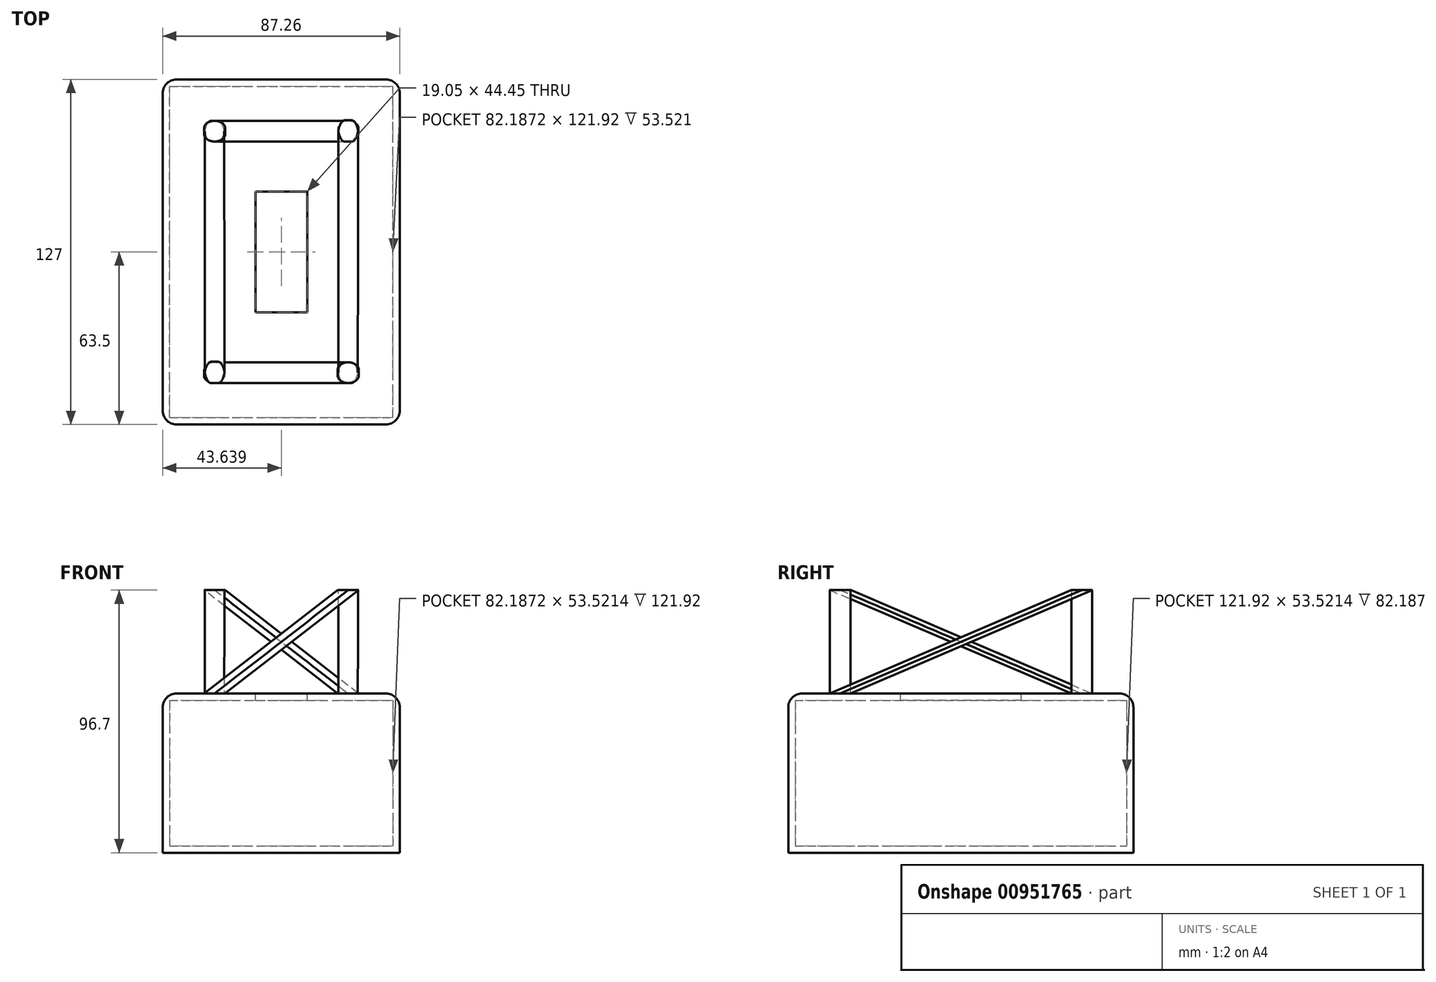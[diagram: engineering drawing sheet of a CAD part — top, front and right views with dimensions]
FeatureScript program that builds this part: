
annotation { "Feature Type Name" : "Feature", "Feature Type Description" : "" }
export const myFeature = defineFeature(function(context is Context, id is Id, definition is map)
    precondition{}
    {
        {
            var Q0;
            Q0=qCreatedBy(makeId("Front.planeOp"),FACE);
            var sketch = newSketch(context, id + "F0", { "sketchPlane" : qUnion([Q0])});
            skLineSegment(sketch, "E0.bottom", {"start": v(-42.36, 35.47) * mm, "end": v(44.9, 35.47) * mm});
            skLineSegment(sketch, "E0.top", {"start": v(-42.36, -23.13) * mm, "end": v(44.9, -23.13) * mm});
            skLineSegment(sketch, "E0.left", {"start": v(-42.36, 35.47) * mm, "end": v(-42.36, -23.13) * mm});
            skLineSegment(sketch, "E0.right", {"start": v(44.9, 35.47) * mm, "end": v(44.9, -23.13) * mm});
            skSolve(sketch);
        }
        {
            var Q0;
            Q0=makeQuery(id+"F0.imprint","IMPRINT",FACE,{"disambiguationData":[TD([[makeQuery(id+"F0.imprint","IMPRINT",EDGE,{"derivedFrom":sQuery(id+"F0.wireOp",EDGE,"E0.bottom")}),-1.0]])]});
            extrude(context, id + "F1", {"entities" : qUnion([Q0]), "depth" : 127 * mm, "offsetDistance" : 25.4 * mm});
        }
        {
            var Q0;
            Q0=makeQuery(id+"F1.opExtrude","SWEPT_FACE",FACE,{"disambiguationData":[OSD([sQuery(id+"F0.wireOp",EDGE,"E0.bottom")])]});
            var sketch = newSketch(context, id + "F2", { "sketchPlane" : qUnion([Q0])});
            skLineSegment(sketch, "E1.bottom", {"start": v(-8.25, -41.28) * mm, "end": v(10.8, -41.28) * mm});
            skLineSegment(sketch, "E1.top", {"start": v(-8.25, -85.73) * mm, "end": v(10.8, -85.73) * mm});
            skLineSegment(sketch, "E1.left", {"start": v(-8.25, -41.28) * mm, "end": v(-8.25, -85.73) * mm});
            skLineSegment(sketch, "E1.right", {"start": v(10.8, -41.28) * mm, "end": v(10.8, -85.73) * mm});
            skSolve(sketch);
        }
        {
            var Q0;
            Q0=makeQuery(id+"F2.imprint","IMPRINT",FACE,{"disambiguationData":[TD([[makeQuery(id+"F2.imprint","IMPRINT",EDGE,{"derivedFrom":sQuery(id+"F2.wireOp",EDGE,"E1.bottom")}),-1.0]])]});
            extrude(context, id + "F3", {"entities" : qUnion([Q0]), "operationType" : NewBodyOperationType.REMOVE, "oppositeDirection" : true, "depth" : 2.54 * mm, "offsetDistance" : 25.4 * mm});
        }
        {
            var Q0;
            Q0=makeQuery(id+"F3.boolean.opBoolean","COPY",FACE,{"derivedFrom":makeQuery(id+"F3.opExtrude","CAP_FACE",FACE,{"disambiguationData":[OSD([sQuery(id+"F2.wireOp",EDGE,"E1.bottom"),sQuery(id+"F2.wireOp",EDGE,"E1.top"),sQuery(id+"F2.wireOp",EDGE,"E1.left"),sQuery(id+"F2.wireOp",EDGE,"E1.right")])],"isStart":false})});
            shell(context, id + "F4", {"entities" : qUnion([Q0]), "thickness" : 2.54 * mm});
        }
        {
            var Q0;
            Q0=makeQuery(id+"F1.opExtrude","SWEPT_EDGE",EDGE,{"disambiguationData":[OSD([sQuery(id+"F0.wireOp",EDGE,"E0.bottom"),sQuery(id+"F0.wireOp",EDGE,"E0.left")])]});
            var Q1;
            Q1=makeQuery(id+"F1.opExtrude","CAP_EDGE",EDGE,{"disambiguationData":[OSD([sQuery(id+"F0.wireOp",EDGE,"E0.bottom")])],"isStart":false});
            var Q2;
            Q2=makeQuery(id+"F1.opExtrude","SWEPT_EDGE",EDGE,{"disambiguationData":[OSD([sQuery(id+"F0.wireOp",EDGE,"E0.bottom"),sQuery(id+"F0.wireOp",EDGE,"E0.right")])]});
            var Q3;
            Q3=makeQuery(id+"F1.opExtrude","CAP_EDGE",EDGE,{"disambiguationData":[OSD([sQuery(id+"F0.wireOp",EDGE,"E0.bottom")])],"isStart":true});
            var Q4;
            Q4=makeQuery(id+"F3.boolean.opBoolean","COPY",EDGE,{"derivedFrom":makeQuery(id+"F3.opExtrude","CAP_EDGE",EDGE,{"disambiguationData":[OSD([sQuery(id+"F2.wireOp",EDGE,"E1.left")])],"isStart":true})});
            var Q5;
            Q5=makeQuery(id+"F3.boolean.opBoolean","COPY",EDGE,{"derivedFrom":makeQuery(id+"F3.opExtrude","CAP_EDGE",EDGE,{"disambiguationData":[OSD([sQuery(id+"F2.wireOp",EDGE,"E1.bottom")])],"isStart":true})});
            var Q6;
            Q6=makeQuery(id+"F3.boolean.opBoolean","COPY",EDGE,{"derivedFrom":makeQuery(id+"F3.opExtrude","CAP_EDGE",EDGE,{"disambiguationData":[OSD([sQuery(id+"F2.wireOp",EDGE,"E1.right")])],"isStart":true})});
            var Q7;
            Q7=makeQuery(id+"F3.boolean.opBoolean","COPY",EDGE,{"derivedFrom":makeQuery(id+"F3.opExtrude","CAP_EDGE",EDGE,{"disambiguationData":[OSD([sQuery(id+"F2.wireOp",EDGE,"E1.top")])],"isStart":true})});
            var Q8;
            Q8=makeQuery(id+"F1.opExtrude","CAP_EDGE",EDGE,{"disambiguationData":[OSD([sQuery(id+"F0.wireOp",EDGE,"E0.left")])],"isStart":false});
            var Q9;
            Q9=makeQuery(id+"F1.opExtrude","CAP_EDGE",EDGE,{"disambiguationData":[OSD([sQuery(id+"F0.wireOp",EDGE,"E0.right")])],"isStart":false});
            var Q10;
            Q10=makeQuery(id+"F1.opExtrude","CAP_EDGE",EDGE,{"disambiguationData":[OSD([sQuery(id+"F0.wireOp",EDGE,"E0.right")])],"isStart":true});
            var Q11;
            Q11=makeQuery(id+"F1.opExtrude","CAP_EDGE",EDGE,{"disambiguationData":[OSD([sQuery(id+"F0.wireOp",EDGE,"E0.left")])],"isStart":true});
            fillet(context, id + "F5", {"entities" : qUnion([Q0, Q1, Q2, Q3, Q4, Q5, Q6, Q7, Q8, Q9, Q10, Q11]), "radius" : 5.08 * mm, "tangentPropagation" : true, "allowEdgeOverflow" : false});
        }
        {
            var Q0;
            Q0=makeQuery(id+"F1.opExtrude","SWEPT_FACE",FACE,{"disambiguationData":[OSD([sQuery(id+"F0.wireOp",EDGE,"E0.bottom")])]});
            var sketch = newSketch(context, id + "F6", { "sketchPlane" : qUnion([Q0])});
            skLineSegment(sketch, "E2.bottom", {"start": v(-19.5, -22.86) * mm, "end": v(-27.12, -22.86) * mm});
            skLineSegment(sketch, "E2.top", {"start": v(-19.5, -15.24) * mm, "end": v(-27.12, -15.24) * mm});
            skLineSegment(sketch, "E2.left", {"start": v(-19.5, -22.86) * mm, "end": v(-19.5, -15.24) * mm});
            skLineSegment(sketch, "E2.right", {"start": v(-27.12, -22.86) * mm, "end": v(-27.12, -15.24) * mm});
            skPoint(sketch, "E2.middle", {"position": v(-23.31, -19.05) * mm});
            skPoint(sketch, "E3.middle.positionSnap0", {"position": v(-23.31, -15.24) * mm});
            skPoint(sketch, "E3.centerSnap0", {"position": v(-23.31, -15.24) * mm});
            skLineSegment(sketch, "E4.bottom", {"start": v(29.66, -111.76) * mm, "end": v(22.04, -111.76) * mm});
            skLineSegment(sketch, "E4.top", {"start": v(29.66, -104.14) * mm, "end": v(22.04, -104.14) * mm});
            skLineSegment(sketch, "E4.left", {"start": v(29.66, -111.76) * mm, "end": v(29.66, -104.14) * mm});
            skLineSegment(sketch, "E4.right", {"start": v(22.04, -111.76) * mm, "end": v(22.04, -104.14) * mm});
            skPoint(sketch, "E4.middle", {"position": v(25.85, -107.95) * mm});
            skLineSegment(sketch, "E5.bottom", {"start": v(-19.5, -111.76) * mm, "end": v(-27.12, -111.76) * mm});
            skLineSegment(sketch, "E5.top", {"start": v(-19.5, -104.14) * mm, "end": v(-27.12, -104.14) * mm});
            skLineSegment(sketch, "E5.left", {"start": v(-19.5, -111.76) * mm, "end": v(-19.5, -104.14) * mm});
            skLineSegment(sketch, "E5.right", {"start": v(-27.12, -111.76) * mm, "end": v(-27.12, -104.14) * mm});
            skPoint(sketch, "E5.middle", {"position": v(-23.31, -107.95) * mm});
            skLineSegment(sketch, "E6.bottom", {"start": v(22.04, -15.24) * mm, "end": v(29.66, -15.24) * mm});
            skLineSegment(sketch, "E6.top", {"start": v(22.04, -22.86) * mm, "end": v(29.66, -22.86) * mm});
            skLineSegment(sketch, "E6.left", {"start": v(22.04, -15.24) * mm, "end": v(22.04, -22.86) * mm});
            skLineSegment(sketch, "E6.right", {"start": v(29.66, -15.24) * mm, "end": v(29.66, -22.86) * mm});
            skSolve(sketch);
        }
        {
            var Q0;
            Q0=makeQuery(id+"F6.imprint","IMPRINT",FACE,{"disambiguationData":[TD([[makeQuery(id+"F6.imprint","IMPRINT",EDGE,{"derivedFrom":sQuery(id+"F6.wireOp",EDGE,"E2.bottom")}),1.0]])]});
            cPlane(context, id + "F7", {"entities" : qUnion([Q0]), "cplaneType" : CPlaneType.OFFSET, "offset" : 38.1 * mm, "width" : 152.4 * mm, "height" : 152.4 * mm});
        }
        {
            var Q0;
            Q0=qCreatedBy(id+"F7.planeOp",FACE);
            var sketch = newSketch(context, id + "F8", { "sketchPlane" : qUnion([Q0])});
            skLineSegment(sketch, "E7.bottom", {"start": v(-27.07, -15.19) * mm, "end": v(-19.39, -15.19) * mm});
            skLineSegment(sketch, "E7.top", {"start": v(-27.07, -22.87) * mm, "end": v(-19.39, -22.87) * mm});
            skLineSegment(sketch, "E7.left", {"start": v(-27.07, -15.19) * mm, "end": v(-27.07, -22.87) * mm});
            skLineSegment(sketch, "E7.right", {"start": v(-19.39, -15.19) * mm, "end": v(-19.39, -22.87) * mm});
            skLineSegment(sketch, "E8.bottom", {"start": v(22.08, -15.03) * mm, "end": v(29.76, -15.03) * mm});
            skLineSegment(sketch, "E8.top", {"start": v(22.08, -22.87) * mm, "end": v(29.76, -22.87) * mm});
            skLineSegment(sketch, "E8.left", {"start": v(22.08, -15.03) * mm, "end": v(22.08, -22.87) * mm});
            skLineSegment(sketch, "E8.right", {"start": v(29.76, -15.03) * mm, "end": v(29.76, -22.87) * mm});
            skLineSegment(sketch, "E9.bottom", {"start": v(29.76, -104.1) * mm, "end": v(22.08, -104.1) * mm});
            skLineSegment(sketch, "E9.top", {"start": v(29.76, -111.79) * mm, "end": v(22.08, -111.79) * mm});
            skLineSegment(sketch, "E9.left", {"start": v(29.76, -104.1) * mm, "end": v(29.76, -111.79) * mm});
            skLineSegment(sketch, "E9.right", {"start": v(22.08, -104.1) * mm, "end": v(22.08, -111.79) * mm});
            skLineSegment(sketch, "E10.bottom", {"start": v(-19.39, -103.96) * mm, "end": v(-27.07, -103.96) * mm});
            skLineSegment(sketch, "E10.top", {"start": v(-19.39, -111.79) * mm, "end": v(-27.07, -111.79) * mm});
            skLineSegment(sketch, "E10.left", {"start": v(-19.39, -103.96) * mm, "end": v(-19.39, -111.79) * mm});
            skLineSegment(sketch, "E10.right", {"start": v(-27.07, -103.96) * mm, "end": v(-27.07, -111.79) * mm});
            skSolve(sketch);
        }
        {
            var Q1;
            Q1=makeQuery(id+"F8.imprint","IMPRINT",FACE,{"disambiguationData":[TD([[makeQuery(id+"F8.imprint","IMPRINT",EDGE,{"derivedFrom":sQuery(id+"F8.wireOp",EDGE,"E7.bottom")}),-1.0]])]});
            var Q2;
            Q2=makeQuery(id+"F6.imprint","IMPRINT",FACE,{"disambiguationData":[TD([[makeQuery(id+"F6.imprint","IMPRINT",EDGE,{"derivedFrom":sQuery(id+"F6.wireOp",EDGE,"E6.bottom")}),-1.0]])]});
            loft(context, id + "F9", {"operationType" : NewBodyOperationType.ADD, "sheetProfilesArray" : [{ "sheetProfileEntities" : qUnion([Q1]) }, { "sheetProfileEntities" : qUnion([Q2]) }]});
        }
        {
            var Q1;
            Q1=makeQuery(id+"F8.imprint","IMPRINT",FACE,{"disambiguationData":[TD([[makeQuery(id+"F8.imprint","IMPRINT",EDGE,{"derivedFrom":sQuery(id+"F8.wireOp",EDGE,"E8.bottom")}),-1.0]])]});
            var Q2;
            Q2=makeQuery(id+"F6.imprint","IMPRINT",FACE,{"disambiguationData":[TD([[makeQuery(id+"F6.imprint","IMPRINT",EDGE,{"derivedFrom":sQuery(id+"F6.wireOp",EDGE,"E4.bottom")}),-1.0]])]});
            loft(context, id + "F10", {"operationType" : NewBodyOperationType.ADD, "sheetProfilesArray" : [{ "sheetProfileEntities" : qUnion([Q1]) }, { "sheetProfileEntities" : qUnion([Q2]) }]});
        }
        {
            var Q1;
            Q1=makeQuery(id+"F8.imprint","IMPRINT",FACE,{"disambiguationData":[TD([[makeQuery(id+"F8.imprint","IMPRINT",EDGE,{"derivedFrom":sQuery(id+"F8.wireOp",EDGE,"E9.bottom")}),1.0]])]});
            var Q2;
            Q2=makeQuery(id+"F6.imprint","IMPRINT",FACE,{"disambiguationData":[TD([[makeQuery(id+"F6.imprint","IMPRINT",EDGE,{"derivedFrom":sQuery(id+"F6.wireOp",EDGE,"E5.bottom")}),-1.0]])]});
            loft(context, id + "F11", {"operationType" : NewBodyOperationType.ADD, "sheetProfilesArray" : [{ "sheetProfileEntities" : qUnion([Q1]) }, { "sheetProfileEntities" : qUnion([Q2]) }]});
        }
        {
            var Q1;
            Q1=makeQuery(id+"F8.imprint","IMPRINT",FACE,{"disambiguationData":[TD([[makeQuery(id+"F8.imprint","IMPRINT",EDGE,{"derivedFrom":sQuery(id+"F8.wireOp",EDGE,"E10.bottom")}),1.0]])]});
            var Q2;
            Q2=makeQuery(id+"F6.imprint","IMPRINT",FACE,{"disambiguationData":[TD([[makeQuery(id+"F6.imprint","IMPRINT",EDGE,{"derivedFrom":sQuery(id+"F6.wireOp",EDGE,"E2.bottom")}),-1.0]])]});
            loft(context, id + "F12", {"operationType" : NewBodyOperationType.ADD, "sheetProfilesArray" : [{ "sheetProfileEntities" : qUnion([Q1]) }, { "sheetProfileEntities" : qUnion([Q2]) }]});
        }
        {
            var Q0;
            Q0=makeQuery(id+"F11.opLoft","SWEPT_EDGE",EDGE,{"disambiguationData":[OSD([sQuery(id+"F6.wireOp",EDGE,"E5.bottom"),sQuery(id+"F6.wireOp",EDGE,"E5.right"),sQuery(id+"F8.wireOp",EDGE,"E9.top"),sQuery(id+"F8.wireOp",EDGE,"E9.right")])]});
            var Q1;
            Q1=makeQuery(id+"F11.opLoft","SWEPT_EDGE",EDGE,{"disambiguationData":[OSD([sQuery(id+"F6.wireOp",EDGE,"E5.top"),sQuery(id+"F6.wireOp",EDGE,"E5.right"),sQuery(id+"F8.wireOp",EDGE,"E9.bottom"),sQuery(id+"F8.wireOp",EDGE,"E9.right")])]});
            var Q2;
            Q2=makeQuery(id+"F11.opLoft","SWEPT_EDGE",EDGE,{"disambiguationData":[OSD([sQuery(id+"F6.wireOp",EDGE,"E5.bottom"),sQuery(id+"F6.wireOp",EDGE,"E5.left"),sQuery(id+"F8.wireOp",EDGE,"E9.top"),sQuery(id+"F8.wireOp",EDGE,"E9.left")])]});
            var Q3;
            Q3=makeQuery(id+"F11.opLoft","SWEPT_EDGE",EDGE,{"disambiguationData":[OSD([sQuery(id+"F6.wireOp",EDGE,"E5.top"),sQuery(id+"F6.wireOp",EDGE,"E5.left"),sQuery(id+"F8.wireOp",EDGE,"E9.bottom"),sQuery(id+"F8.wireOp",EDGE,"E9.left")])]});
            fillet(context, id + "F13", {"entities" : qUnion([Q0, Q1, Q2, Q3]), "radius" : 2.54 * mm, "tangentPropagation" : true, "allowEdgeOverflow" : false});
        }
        {
            var Q0;
            Q0=makeQuery(id+"F10.opLoft","SWEPT_EDGE",EDGE,{"disambiguationData":[OSD([sQuery(id+"F6.wireOp",EDGE,"E4.bottom"),sQuery(id+"F6.wireOp",EDGE,"E4.left"),sQuery(id+"F8.wireOp",EDGE,"E8.top"),sQuery(id+"F8.wireOp",EDGE,"E8.right")])]});
            var Q1;
            Q1=makeQuery(id+"F10.opLoft","SWEPT_EDGE",EDGE,{"disambiguationData":[OSD([sQuery(id+"F6.wireOp",EDGE,"E4.top"),sQuery(id+"F6.wireOp",EDGE,"E4.left"),sQuery(id+"F8.wireOp",EDGE,"E8.bottom"),sQuery(id+"F8.wireOp",EDGE,"E8.right")])]});
            var Q2;
            Q2=makeQuery(id+"F10.opLoft","SWEPT_EDGE",EDGE,{"disambiguationData":[OSD([sQuery(id+"F6.wireOp",EDGE,"E4.bottom"),sQuery(id+"F6.wireOp",EDGE,"E4.right"),sQuery(id+"F8.wireOp",EDGE,"E8.top"),sQuery(id+"F8.wireOp",EDGE,"E8.left")])]});
            var Q3;
            Q3=makeQuery(id+"F10.opLoft","SWEPT_EDGE",EDGE,{"disambiguationData":[OSD([sQuery(id+"F6.wireOp",EDGE,"E4.top"),sQuery(id+"F6.wireOp",EDGE,"E4.right"),sQuery(id+"F8.wireOp",EDGE,"E8.bottom"),sQuery(id+"F8.wireOp",EDGE,"E8.left")])]});
            fillet(context, id + "F14", {"entities" : qUnion([Q0, Q1, Q2, Q3]), "radius" : 2.54 * mm, "tangentPropagation" : true, "allowEdgeOverflow" : false});
        }
        {
            var Q0;
            Q0=makeQuery(id+"F9.opLoft","SWEPT_EDGE",EDGE,{"disambiguationData":[OSD([sQuery(id+"F6.wireOp",EDGE,"E6.top"),sQuery(id+"F6.wireOp",EDGE,"E6.right"),sQuery(id+"F8.wireOp",EDGE,"E7.top"),sQuery(id+"F8.wireOp",EDGE,"E7.right")])]});
            var Q1;
            Q1=makeQuery(id+"F9.opLoft","SWEPT_EDGE",EDGE,{"disambiguationData":[OSD([sQuery(id+"F6.wireOp",EDGE,"E6.top"),sQuery(id+"F6.wireOp",EDGE,"E6.left"),sQuery(id+"F8.wireOp",EDGE,"E7.top"),sQuery(id+"F8.wireOp",EDGE,"E7.left")])]});
            var Q2;
            Q2=makeQuery(id+"F9.opLoft","SWEPT_EDGE",EDGE,{"disambiguationData":[OSD([sQuery(id+"F6.wireOp",EDGE,"E6.bottom"),sQuery(id+"F6.wireOp",EDGE,"E6.left"),sQuery(id+"F8.wireOp",EDGE,"E7.bottom"),sQuery(id+"F8.wireOp",EDGE,"E7.left")])]});
            var Q3;
            Q3=makeQuery(id+"F9.opLoft","SWEPT_EDGE",EDGE,{"disambiguationData":[OSD([sQuery(id+"F6.wireOp",EDGE,"E6.bottom"),sQuery(id+"F6.wireOp",EDGE,"E6.right"),sQuery(id+"F8.wireOp",EDGE,"E7.bottom"),sQuery(id+"F8.wireOp",EDGE,"E7.right")])]});
            var Q4;
            Q4=makeQuery(id+"F12.opLoft","SWEPT_EDGE",EDGE,{"disambiguationData":[OSD([sQuery(id+"F6.wireOp",EDGE,"E2.top"),sQuery(id+"F6.wireOp",EDGE,"E2.left"),sQuery(id+"F8.wireOp",EDGE,"E10.bottom"),sQuery(id+"F8.wireOp",EDGE,"E10.left")])]});
            var Q5;
            Q5=makeQuery(id+"F12.opLoft","SWEPT_EDGE",EDGE,{"disambiguationData":[OSD([sQuery(id+"F6.wireOp",EDGE,"E2.top"),sQuery(id+"F6.wireOp",EDGE,"E2.right"),sQuery(id+"F8.wireOp",EDGE,"E10.bottom"),sQuery(id+"F8.wireOp",EDGE,"E10.right")])]});
            var Q6;
            Q6=makeQuery(id+"F12.opLoft","SWEPT_EDGE",EDGE,{"disambiguationData":[OSD([sQuery(id+"F6.wireOp",EDGE,"E2.bottom"),sQuery(id+"F6.wireOp",EDGE,"E2.right"),sQuery(id+"F8.wireOp",EDGE,"E10.top"),sQuery(id+"F8.wireOp",EDGE,"E10.right")])]});
            var Q7;
            Q7=makeQuery(id+"F12.opLoft","SWEPT_EDGE",EDGE,{"disambiguationData":[OSD([sQuery(id+"F6.wireOp",EDGE,"E2.bottom"),sQuery(id+"F6.wireOp",EDGE,"E2.left"),sQuery(id+"F8.wireOp",EDGE,"E10.top"),sQuery(id+"F8.wireOp",EDGE,"E10.left")])]});
            fillet(context, id + "F15", {"entities" : qUnion([Q0, Q1, Q2, Q3, Q4, Q5, Q6, Q7]), "radius" : 2.54 * mm, "tangentPropagation" : true, "allowEdgeOverflow" : false});
        }
    });
